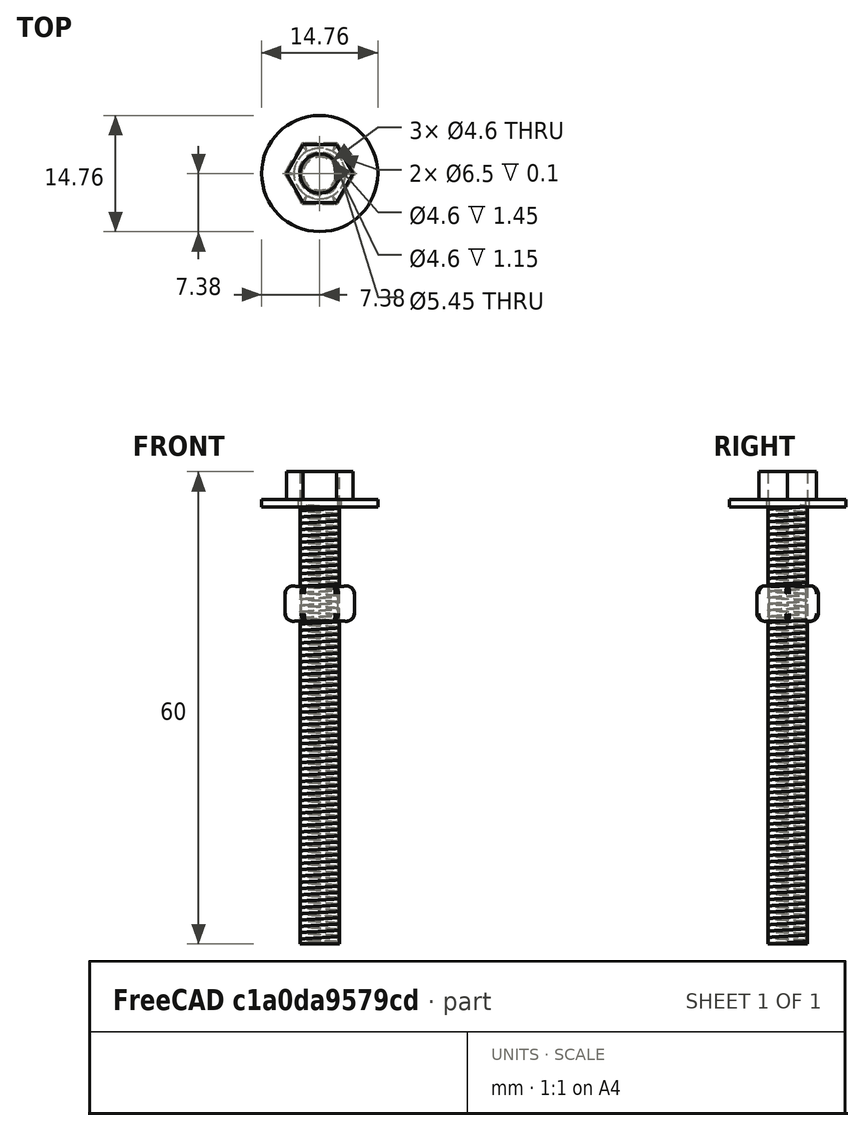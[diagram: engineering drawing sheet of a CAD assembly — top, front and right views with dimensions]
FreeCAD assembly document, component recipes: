
FREECAD ASSEMBLY — COMPONENT RECIPES ("Counterbore2x_5_x_60_mm")

This assembly document has 4 components, labeled P0..P3 below (a component is one placed body or linked part). 4 of them carry a construction recipe — the FreeCAD feature program that regenerates the part from scratch, quoted from this document or its linked companion documents; the rest are supplied as boundary geometry only. No exploded tour is included for this assembly.
COMPONENT P0 — recipe-attached ("copy, Thread, Body", modeled in this document).
Construction recipe (the document's own serialized feature program — sketch geometry with constraints, then the solid features built on it; lengths are millimeters unless a unit is written):

FEATURE [PartDesign::Body] Body004  label="copy, Thread, Body"
  AllowCompound = true
  Origin = -> Origin009
  Tip = -> AdditiveHelix
COMPONENT P1 — recipe-attached ("Washer 2, Part", modeled in this document).
Construction recipe (the document's own serialized feature program — sketch geometry with constraints, then the solid features built on it; lengths are millimeters unless a unit is written):

FEATURE [Sketcher::SketchObject] Sketch004
  ArcFitTolerance = 0
  AttachmentSupport = -> [XY_Plane003]
  ExternalTypes = [0]
  FullyConstrained = true
  MakeInternals = false
  MapMode = 5
  _ExternalGeoVersion = 0
  sketch-geometry (1):
    g0: Circle CenterX=0 CenterY=0 CenterZ=0 NormalX=0 NormalY=0 NormalZ=1 AngleXU=0 Radius=7.375
  constraints (2):
    c: Coincident(g0,g-1)
    c: Diameter(g0) = 14.75
FEATURE [PartDesign::Pad] Pad002  label="Washer"
  Direction = (0,0,1)
  Length = 1
  Length2 = 10
  Profile = -> Sketch004
  ReferenceAxis = -> Sketch004 [N_Axis]
  SideType = 0
  Suppressed = false
  Type = 0
  Type2 = 0
FEATURE [Sketcher::SketchObject] Sketch006
  ArcFitTolerance = 0
  AttachmentSupport = -> [Pad002]
  ExternalTypes = [0]
  FullyConstrained = true
  MakeInternals = false
  MapMode = 5
  Placement = pos=(0,0,1) rot=(0,0,1;0rad)
  _ExternalGeoVersion = 0
  sketch-geometry (1):
    g0: Circle CenterX=0 CenterY=0 CenterZ=0 NormalX=0 NormalY=0 NormalZ=1 AngleXU=0 Radius=2.725
  constraints (2):
    c: Coincident(g0,g-1)
    c: Diameter(g0) = 5.45
FEATURE [PartDesign::Hole] Hole
  BaseFeature = -> Pad002
  BaseProfileType = 6
  CustomThreadClearance = 0
  Depth = 2
  DepthType = 0
  Diameter = 5.45
  DrillForDepth = false
  DrillPoint = 1
  DrillPointAngle = 118
  HoleCutCountersinkAngle = 90
  HoleCutCustomValues = false
  HoleCutDepth = 0
  HoleCutDiameter = 6.1
  HoleCutType = 0
  ModelThread = false
  Profile = -> Sketch006
  Suppressed = false
  Tapered = false
  TaperedAngle = 90
  ThreadClass = 0
  ThreadDepth = 2
  ThreadDepthType = 0
  ThreadDiameter = 5.45
  ThreadDirection = 0
  ThreadFit = 0
  ThreadSize = 0
  ThreadType = 0
  Threaded = false
  UseCustomThreadClearance = false
FEATURE [PartDesign::Body] Body002  label="Washer, Body"
  AllowCompound = true
  Group = -> [Sketch004,Pad002,Sketch006,Hole]
  Origin = -> Origin003
  Placement = pos=(0,0,55.5) rot=(0,0,1;0rad)
  Tip = -> Hole
  expr: .Placement.Base.z = Spreadsheet.threadheight + Spreadsheet.threadfree - 1
COMPONENT P2 — recipe-attached ("Thread, Part", modeled in this document).
Construction recipe (the document's own serialized feature program — sketch geometry with constraints, then the solid features built on it; lengths are millimeters unless a unit is written):

FEATURE [Sketcher::SketchObject] Sketch  label="Core, Pattern"
  ArcFitTolerance = 0
  AttachmentSupport = -> [XZ_Plane]
  ExternalTypes = [0]
  FullyConstrained = true
  MakeInternals = false
  MapMode = 5
  Placement = pos=(0,0,0) rot=(1,0,0;1.5708rad)
  _ExternalGeoVersion = 0
  expr: Constraints[13] = Spreadsheet.boltradius
  expr: Constraints[6] = Spreadsheet.boltheight - Spreadsheet.headheight
  sketch-geometry (5):
    g0: LineSegment StartX=0 StartY=0 StartZ=0 EndX=2.1 EndY=0 EndZ=0
    g1: LineSegment StartX=2.3 StartY=0.2 StartZ=0 EndX=2.3 EndY=56.5 EndZ=0
    g2: LineSegment StartX=2.3 StartY=56.5 StartZ=0 EndX=0 EndY=56.5 EndZ=0
    g3: LineSegment StartX=0 StartY=56.5 StartZ=0 EndX=0 EndY=0 EndZ=0
    g4: LineSegment StartX=2.1 StartY=0 StartZ=0 EndX=2.3 EndY=0.2 EndZ=0
  constraints (14):
    c: Coincident(g-1,g0)
    c: Vertical(g1)
    c: PointOnObject(g2,g-2)
    c: Horizontal(g2)
    c: Coincident(g2,g3)
    c: Coincident(g3,g0)
    c: DistanceY(g3,g3) = 56.5
    c: PointOnObject(g0,g-1)
    c: Coincident(g4,g0)
    c: Coincident(g4,g1)
    c: DistanceX(g0,g1) = 0.2
    c: DistanceY(g0,g1) = 0.2
    c: Coincident(g1,g2)
    c: DistanceX(g0,g1) = 2.3
FEATURE [PartDesign::Revolution] Revolution  label="Core"
  Angle = 360
  Angle2 = 0
  Axis = (0,2e-16,1)
  Base = (0,0,0)
  FuseOrder = 0
  Placement = pos=(0,0,0) rot=(1,0,0;1.5708rad)
  Profile = -> Sketch
  ReferenceAxis = -> Sketch [V_Axis]
  Reversed = true
  Suppressed = false
  Type = 0
FEATURE [Sketcher::SketchObject] Sketch001  label="Thread, Pattern"
  ArcFitTolerance = 0
  AttachmentSupport = -> [XZ_Plane]
  ExternalTypes = [0]
  FullyConstrained = true
  MakeInternals = false
  MapMode = 5
  Placement = pos=(0,0,0) rot=(1,0,0;1.5708rad)
  _ExternalGeoVersion = 0
  expr: Constraints[3] = Spreadsheet.boltradius
  sketch-geometry (3):
    g0: LineSegment StartX=2.3 StartY=0.15 StartZ=0 EndX=2.5 EndY=0.2 EndZ=0
    g1: LineSegment StartX=2.5 StartY=0.2 StartZ=0 EndX=2.3 EndY=0.25 EndZ=0
    g2: LineSegment StartX=2.3 StartY=0.25 StartZ=0 EndX=2.3 EndY=0.15 EndZ=0
  constraints (9):
    c: Coincident(g0,g1)
    c: Equal(g0,g1)
    c: DistanceY(g-1,g0) = 0.2
    c: DistanceX(g-1,g0) = 2.3
    c: DistanceX(g0,g0) = 0.2
    c: DistanceY(g0,g1) = 0.1
    c: Vertical(g1,g0)
    c: Coincident(g2,g1)
    c: Coincident(g2,g0)
FEATURE [PartDesign::AdditiveHelix] AdditiveHelix  label="Thread"
  Angle = 0
  Axis = (0,2e-16,1)
  Base = (0,0,0)
  BaseFeature = -> Revolution
  Growth = 0
  HasBeenEdited = true
  Height = 55.5
  LeftHanded = false
  Mode = 0
  Outside = false
  Pitch = 0.8
  Placement = pos=(0,0,0) rot=(1,0,0;1.5708rad)
  Profile = -> Sketch001
  ReferenceAxis = -> Sketch001 [V_Axis]
  Suppressed = false
  Tolerance = 0.1
  Turns = 69.375
  expr: Height = Spreadsheet.threadheight
  expr: Pitch = Spreadsheet.threadjump
FEATURE [PartDesign::Body] Body  label="Thread, Body"
  AllowCompound = true
  Group = -> [Sketch,Revolution,Sketch001,AdditiveHelix]
  Origin = -> Origin
  Tip = -> AdditiveHelix
COMPONENT P3 — recipe-attached ("Head, Part", modeled in this document).
Construction recipe (the document's own serialized feature program — sketch geometry with constraints, then the solid features built on it; lengths are millimeters unless a unit is written):

FEATURE [Sketcher::SketchObject] Sketch005
  ArcFitTolerance = 0
  AttachmentSupport = -> [XY_Plane008]
  ExternalTypes = [0]
  FullyConstrained = true
  MakeInternals = false
  MapMode = 5
  _ExternalGeoVersion = 0
  expr: Constraints[19] = Spreadsheet.headradius
  sketch-geometry (7):
    g0: LineSegment StartX=2.1125 StartY=-3.65896 StartZ=0 EndX=4.225 EndY=-4e-16 EndZ=0
    g1: LineSegment StartX=4.225 StartY=-4e-16 StartZ=0 EndX=2.1125 EndY=3.65896 EndZ=0
    g2: LineSegment StartX=2.1125 StartY=3.65896 StartZ=0 EndX=-2.1125 EndY=3.65896 EndZ=0
    g3: LineSegment StartX=-2.1125 StartY=3.65896 StartZ=0 EndX=-4.225 EndY=0 EndZ=0
    g4: LineSegment StartX=-4.225 StartY=0 StartZ=0 EndX=-2.1125 EndY=-3.65896 EndZ=0
    g5: LineSegment StartX=-2.1125 StartY=-3.65896 StartZ=0 EndX=2.1125 EndY=-3.65896 EndZ=0
    g6: Circle [constr] CenterX=0 CenterY=0 CenterZ=0 NormalX=0 NormalY=0 NormalZ=1 AngleXU=0 Radius=4.225
  constraints (16):
    c: Coincident(g0,g1)
    c: Coincident(g1,g2)
    c: Coincident(g2,g3)
    c: Coincident(g3,g4)
    c: Coincident(g4,g5)
    c: Coincident(g5,g0)
    c: Equal(g0, g1-g5) x5
    c: PointOnObject(g0,g6)
    c: PointOnObject(g1,g6)
    c: PointOnObject(g2,g6)
    c: PointOnObject(g3,g6)
    c: PointOnObject(g4,g6)
    c: PointOnObject(g5,g6)
    c: Coincident(g6,g-1)
    c: PointOnObject(g3,g-1)
    c: DistanceX(g6,g0) = 4.225
FEATURE [PartDesign::Pad] Pad  label="Head"
  Direction = (0,0,1)
  Length = 3.5
  Length2 = 10
  Profile = -> Sketch005
  ReferenceAxis = -> Sketch005 [N_Axis]
  SideType = 0
  Suppressed = false
  Type = 0
  Type2 = 0
  expr: Length = Spreadsheet.headheight
FEATURE [PartDesign::Body] Body003  label="Head, Body"
  AllowCompound = true
  Group = -> [Sketch005,Pad]
  Origin = -> Origin008
  Placement = pos=(0,0,56.5) rot=(0,0,1;0rad)
  Tip = -> Pad
  expr: .Placement.Base.z = Spreadsheet.threadheight + Spreadsheet.threadfree
PROVENANCE & LICENSES
A FreeCAD (.FCStd) document from a public repository crawl; recipes are the document's own serialized feature recipes (and, for linked parts, companion documents' recipes).
License: mit.
